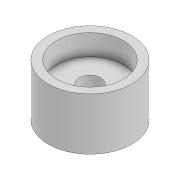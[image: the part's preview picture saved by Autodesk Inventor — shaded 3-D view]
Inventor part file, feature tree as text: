
AUTODESK INVENTOR PART (.ipt)
format: ipt  version: 2020 (Build 240168000, 168)  size: 107,520 bytes
history: native  units: mm
features: extrude x4, sketch x4
ambient origin geometry x8: Origin, YZ Plane, XZ Plane, XY Plane, X Axis, Y Axis, Z Axis, Center Point
bodies: Solid1 (feature_tree)
feature tree (8):
  extrude  "Extrusion1"  Depth=15.0mm TaperAngle=0.0deg
  extrude  "Extrusion2"  Depth=6.0mm TaperAngle=0.0deg
  extrude  "Extrusion3"  Depth=6.0mm TaperAngle=0.0deg
  extrude  "Extrusion4"  Depth=6.0mm TaperAngle=0.0deg
  sketch  "Sketch1"  dims[d1=24.0mm d2=15.0mm d3=0.0mm]
  sketch  "Sketch2"  dims[d4=19.2mm d5=6.0mm d6=0.0mm]
  sketch  "Sketch3"  dims[d7=19.2mm d8=6.0mm d9=0.0mm]
  sketch  "Sketch4"  dims[d10=6.2mm d11=6.0mm d12=0.0mm]
